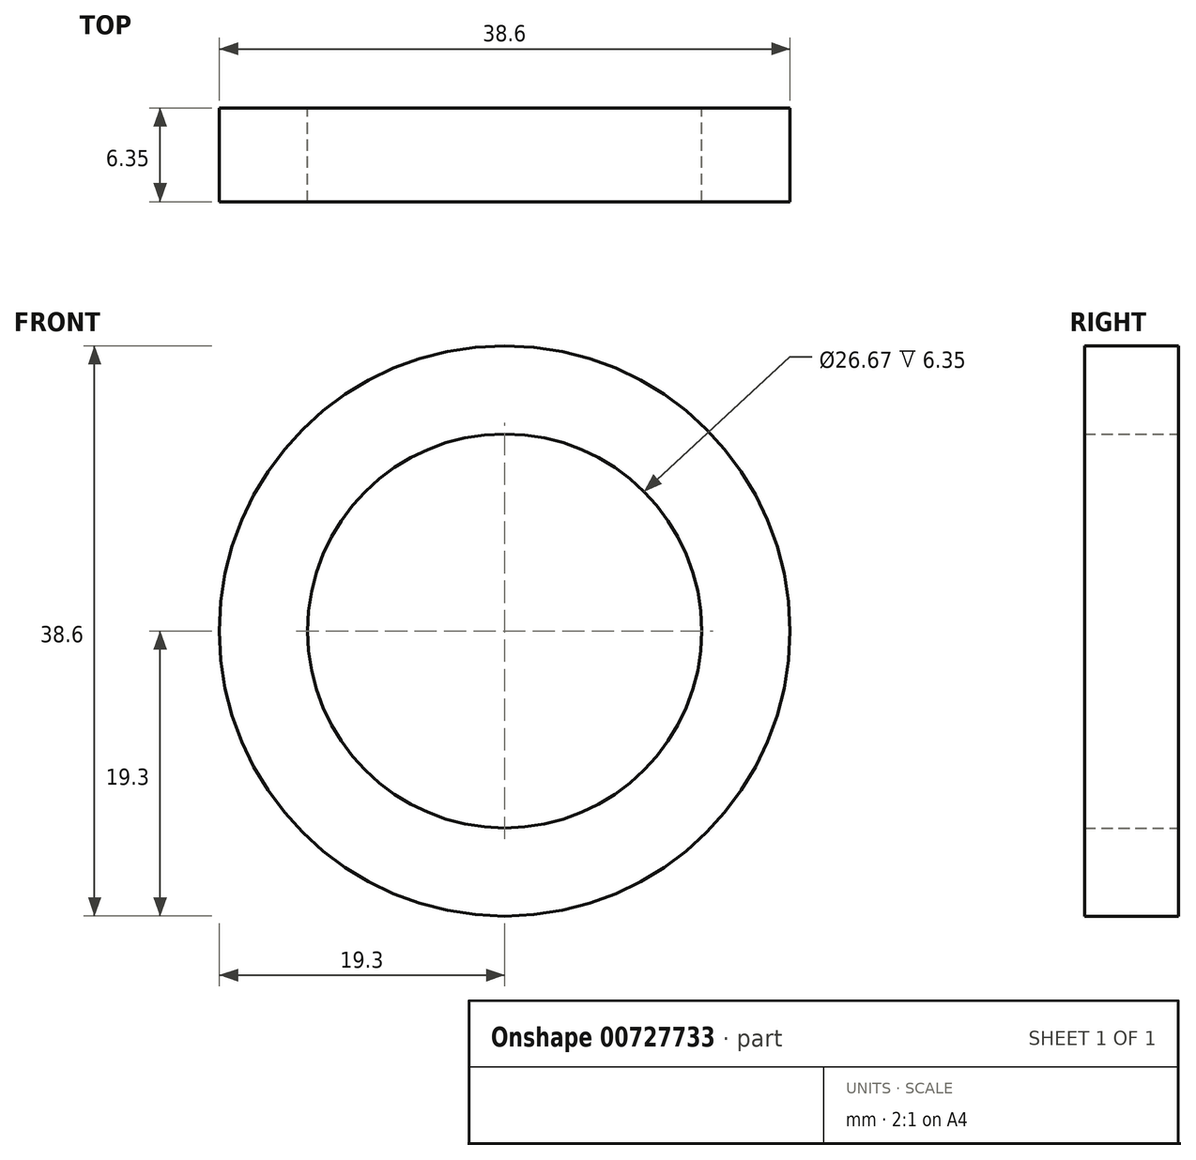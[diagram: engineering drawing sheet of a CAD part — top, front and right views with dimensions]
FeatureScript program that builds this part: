
annotation { "Feature Type Name" : "Feature", "Feature Type Description" : "" }
export const myFeature = defineFeature(function(context is Context, id is Id, definition is map)
    precondition{}
    {
        {
            var Q0;
            Q0=qCreatedBy(makeId("Front.planeOp"),FACE);
            var sketch = newSketch(context, id + "F0", { "sketchPlane" : qUnion([Q0])});
            skCircle(sketch, "E0", {"center": v(0, 0) * mm, "radius": 19.3 * mm});
            skCircle(sketch, "E1", {"center": v(0, 0) * mm, "radius": 13.34 * mm});
            skSolve(sketch);
        }
        {
            var Q0;
            Q0 = qSketchRegion(id + "F0", true);
            extrude(context, id + "F1", {"entities" : qUnion([Q0]), "depth" : 6.35 * mm, "offsetDistance" : 25.4 * mm});
        }
    });
